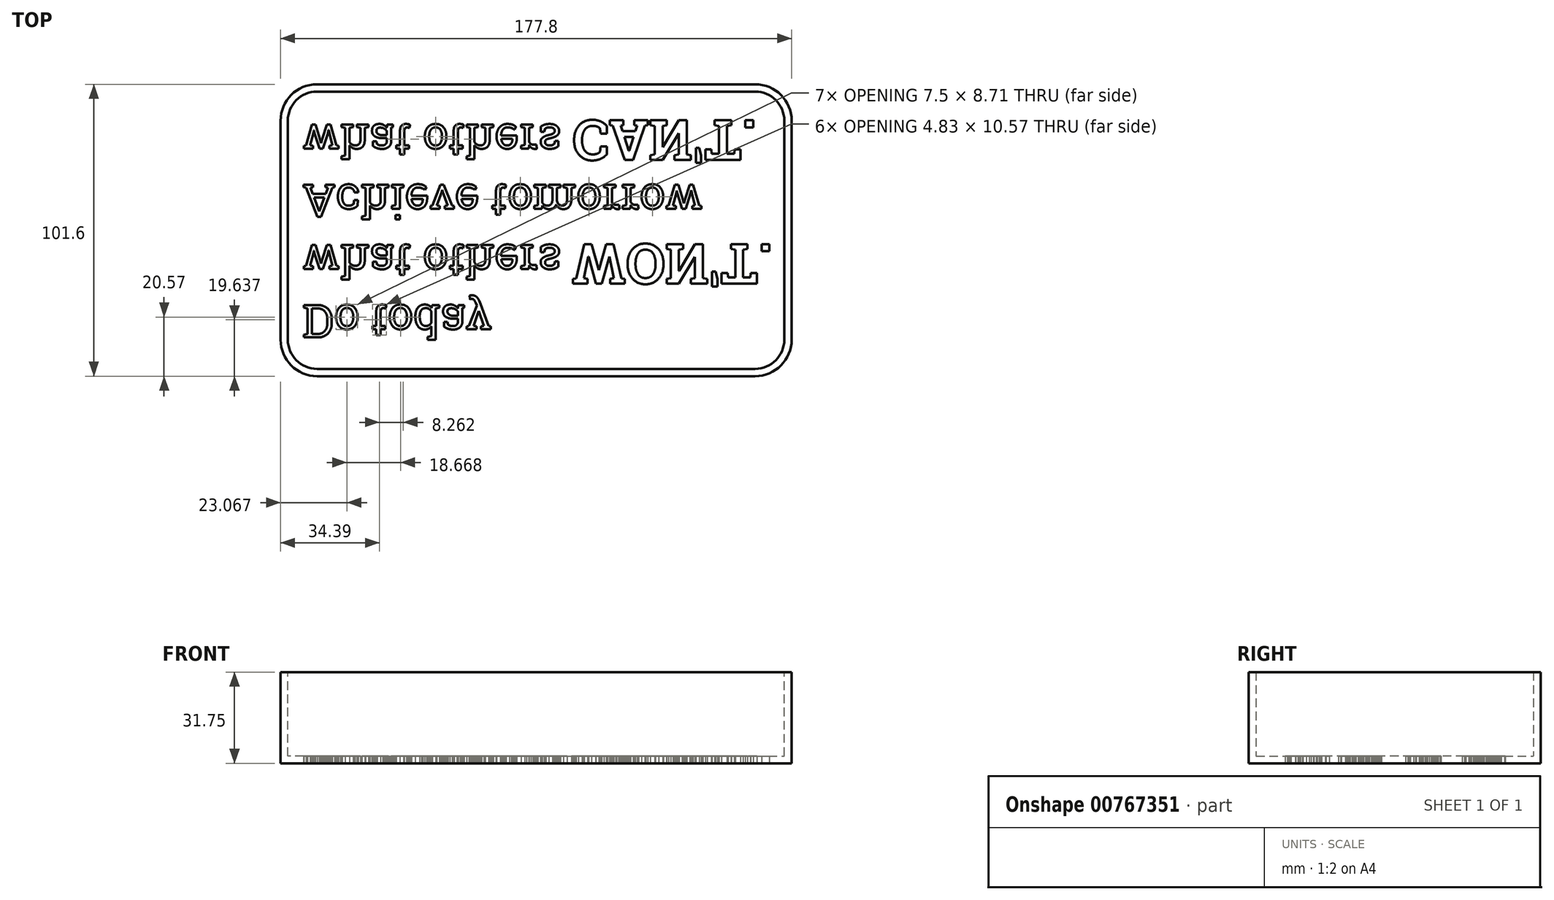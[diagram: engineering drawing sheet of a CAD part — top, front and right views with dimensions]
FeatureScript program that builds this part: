
annotation { "Feature Type Name" : "Feature", "Feature Type Description" : "" }
export const myFeature = defineFeature(function(context is Context, id is Id, definition is map)
    precondition{}
    {
        {
            var Q0;
            Q0=qCreatedBy(makeId("Top.planeOp"),FACE);
            var sketch = newSketch(context, id + "F0", { "sketchPlane" : qUnion([Q0])});
            skLineSegment(sketch, "E0.bottom", {"start": v(-88.9, 50.8) * mm, "end": v(88.9, 50.8) * mm});
            skLineSegment(sketch, "E0.top", {"start": v(-88.9, -50.8) * mm, "end": v(88.9, -50.8) * mm});
            skLineSegment(sketch, "E0.left", {"start": v(-88.9, 50.8) * mm, "end": v(-88.9, -50.8) * mm});
            skLineSegment(sketch, "E0.right", {"start": v(88.9, 50.8) * mm, "end": v(88.9, -50.8) * mm});
            skPoint(sketch, "E0.middle", {"position": v(0, 0) * mm});
            skSolve(sketch);
        }
        {
            var Q0;
            Q0=qSketchRegion(id+"F0",true);
            extrude(context, id + "F1", {"entities" : qUnion([Q0]), "oppositeDirection" : true, "depth" : 31.75 * mm, "offsetDistance" : 25.4 * mm});
        }
        {
            var Q0;
            Q0=makeQuery(id+"F1.opExtrude","SWEPT_EDGE",EDGE,{"disambiguationData":[OSD([sQuery(id+"F0.wireOp",EDGE,"E0.bottom"),sQuery(id+"F0.wireOp",EDGE,"E0.right")])]});
            var Q1;
            Q1=makeQuery(id+"F1.opExtrude","SWEPT_EDGE",EDGE,{"disambiguationData":[OSD([sQuery(id+"F0.wireOp",EDGE,"E0.bottom"),sQuery(id+"F0.wireOp",EDGE,"E0.left")])]});
            var Q2;
            Q2=makeQuery(id+"F1.opExtrude","SWEPT_EDGE",EDGE,{"disambiguationData":[OSD([sQuery(id+"F0.wireOp",EDGE,"E0.top"),sQuery(id+"F0.wireOp",EDGE,"E0.right")])]});
            var Q3;
            Q3=makeQuery(id+"F1.opExtrude","SWEPT_EDGE",EDGE,{"disambiguationData":[OSD([sQuery(id+"F0.wireOp",EDGE,"E0.top"),sQuery(id+"F0.wireOp",EDGE,"E0.left")])]});
            fillet(context, id + "F2", {"entities" : qUnion([Q0, Q1, Q2, Q3]), "radius" : 12.7 * mm, "tangentPropagation" : true, "allowEdgeOverflow" : false});
        }
        {
            var Q0;
            Q0=makeQuery(id+"F1.opExtrude","CAP_FACE",FACE,{"disambiguationData":[OSD([sQuery(id+"F0.wireOp",EDGE,"E0.bottom"),sQuery(id+"F0.wireOp",EDGE,"E0.top"),sQuery(id+"F0.wireOp",EDGE,"E0.left"),sQuery(id+"F0.wireOp",EDGE,"E0.right")])],"isStart":true});
            shell(context, id + "F3", {"entities" : qUnion([Q0]), "thickness" : 2.54 * mm});
        }
        {
            var Q0;
            Q0=makeQuery(id+"F1.opExtrude","CAP_FACE",FACE,{"disambiguationData":[OSD([sQuery(id+"F0.wireOp",EDGE,"E0.bottom"),sQuery(id+"F0.wireOp",EDGE,"E0.top"),sQuery(id+"F0.wireOp",EDGE,"E0.left"),sQuery(id+"F0.wireOp",EDGE,"E0.right")])],"isStart":false});
            var sketch = newSketch(context, id + "F4", { "sketchPlane" : qUnion([Q0])});
            skText(sketch, "E1", { "text": "Do today \nwhat others \nAchieve tomorrow \nwhat others ", "fontName": "RobotoSlab-Regular.ttf"});
            skText(sketch, "E2", { "text": "WON\'T.", "fontName": "RobotoSlab-Bold.ttf"});
            skText(sketch, "E3", { "text": "CAN\'T.", "fontName": "RobotoSlab-Bold.ttf"});
            const initialGuessF4  = {"E1": [-0.08128, 0.02604, 1, 0, 0.01143], "E2": [0.0125, 0.00483, 1, 0, 0.01397], "E3": [0.01274, -0.03824, 1, 0, 0.01397]};
            skSetInitialGuess(sketch, initialGuessF4);
            skSolve(sketch);
        }
        {
            var Q0;
            Q0=qSketchRegion(id+"F4",true);
            extrude(context, id + "F5", {"entities" : qUnion([Q0]), "operationType" : NewBodyOperationType.REMOVE, "oppositeDirection" : true, "depth" : 25.4 * mm, "offsetDistance" : 25.4 * mm});
        }
    });
